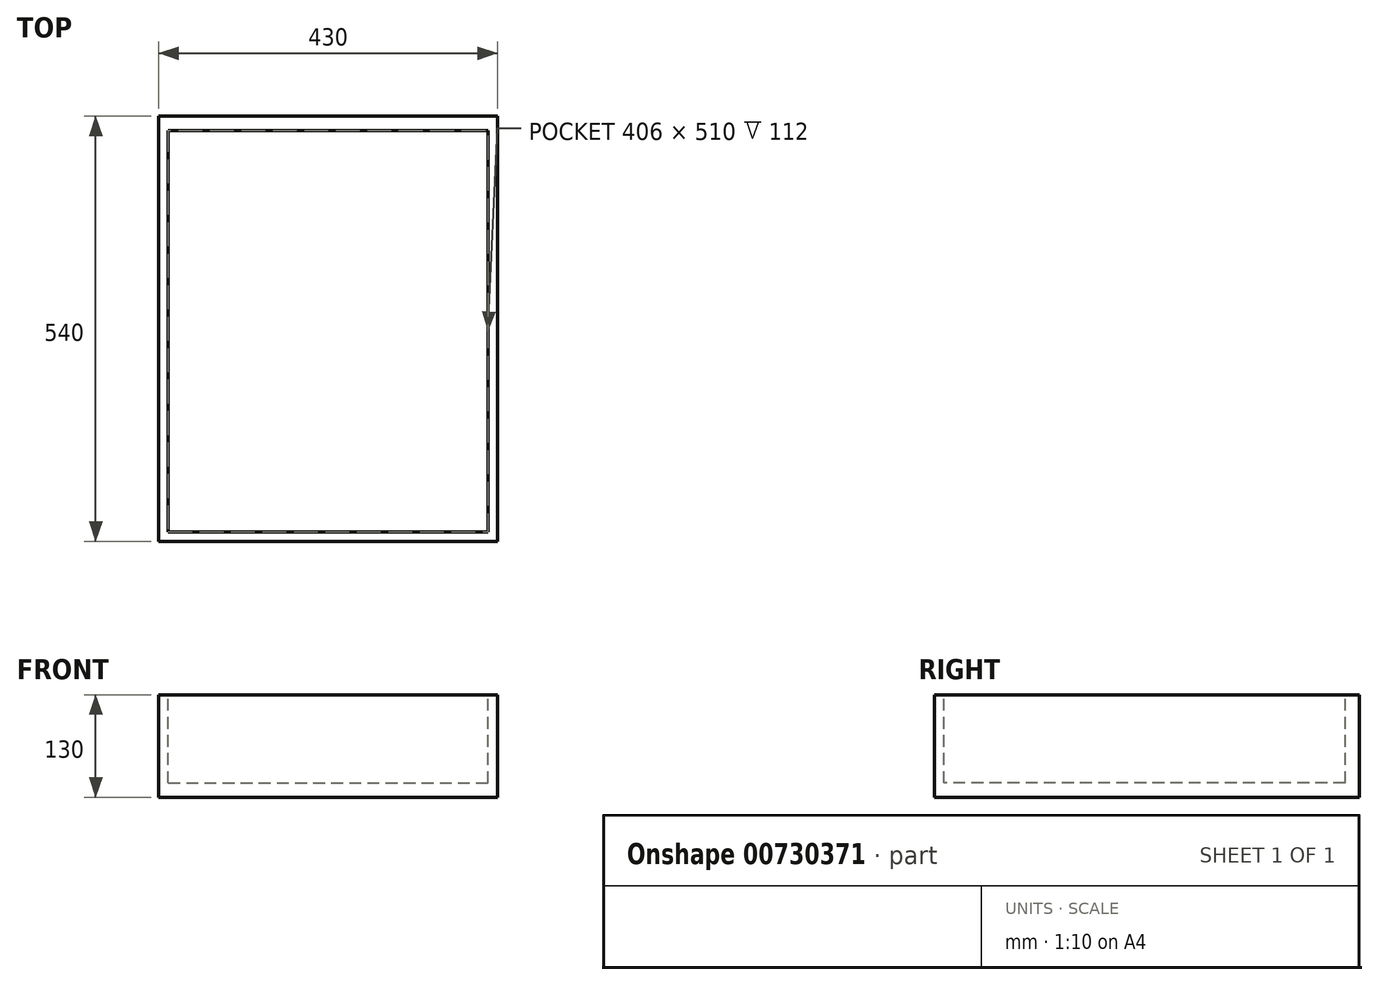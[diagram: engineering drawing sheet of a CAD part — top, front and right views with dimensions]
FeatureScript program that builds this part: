
annotation { "Feature Type Name" : "Feature", "Feature Type Description" : "" }
export const myFeature = defineFeature(function(context is Context, id is Id, definition is map)
    precondition{}
    {
        {
            var Q0;
            Q0=qCreatedBy(makeId("Front.planeOp"),FACE);
            var sketch = newSketch(context, id + "F0", { "sketchPlane" : qUnion([Q0])});
            skLineSegment(sketch, "E0.bottom", {"start": v(-215, 65) * mm, "end": v(215, 65) * mm});
            skLineSegment(sketch, "E0.top", {"start": v(-215, -65) * mm, "end": v(215, -65) * mm});
            skLineSegment(sketch, "E0.left", {"start": v(-215, 65) * mm, "end": v(-215, -65) * mm});
            skLineSegment(sketch, "E0.right", {"start": v(215, 65) * mm, "end": v(215, -65) * mm});
            skPoint(sketch, "E0.middle", {"position": v(0, 0) * mm});
            skSolve(sketch);
        }
        {
            var Q0;
            Q0 = qSketchRegion(id + "F0", true);
            extrude(context, id + "F1", {"entities" : qUnion([Q0]), "depth" : 540 * mm, "offsetDistance" : 25 * mm});
        }
        {
            var Q0;
            Q0=makeQuery(id+"F1.opExtrude","SWEPT_FACE",FACE,{"disambiguationData":[OSD([sQuery(id+"F0.wireOp",EDGE,"E0.bottom")])]});
            var sketch = newSketch(context, id + "F2", { "sketchPlane" : qUnion([Q0])});
            skLineSegment(sketch, "E1.bottom", {"start": v(-203, -18) * mm, "end": v(203, -18) * mm});
            skLineSegment(sketch, "E1.top", {"start": v(-203, -528) * mm, "end": v(203, -528) * mm});
            skLineSegment(sketch, "E1.left", {"start": v(-203, -18) * mm, "end": v(-203, -528) * mm});
            skLineSegment(sketch, "E1.right", {"start": v(203, -18) * mm, "end": v(203, -528) * mm});
            skPoint(sketch, "E1.middle", {"position": v(0, -273) * mm});
            skSolve(sketch);
        }
        {
            var Q0;
            Q0 = qSketchRegion(id + "F2", true);
            extrude(context, id + "F3", {"entities" : qUnion([Q0]), "operationType" : NewBodyOperationType.REMOVE, "oppositeDirection" : true, "depth" : 112 * mm, "offsetDistance" : 25 * mm});
        }
    });
